# Revit family: FP-Revit20-RS32A72UI-FrenchDoorFridgeFreezer-0-90005071A-US-CA
name_source: partatom
category: Specialty Equipment
units: mm (PartAtom-declared; Revit-internal decimal feet)

## family parameters
Always vertical = Yes
Cut with Voids When Loaded = Yes
OmniClass Number = 23.40.40.11.11.17
OmniClass Title = Refrigerator-Freezer
Part Type = Normal
Room Calculation Point = No
Round Connector Dimension = Use Diameter
Shared = No
Work Plane-Based = No

## types (1)
- FP-Revit20-RS32A72UI-FrenchDoorFridgeFreezer-0-90005071A-US-CA
    Cavity - Depth = 635 mm  [stored 2.08333 ft]
    Cavity - Height = 1829 mm  [stored 6.00066 ft]
    Cavity - Width = 813 mm  [stored 2.66732 ft]
    Chassis - Depth = 561 mm
    Chassis - Height = 1788 mm
    Chassis - Width = 790 mm  [stored 2.59186 ft]
    Connector Description - Electrical = 115 V, 60 Hz, 10 A circuit
    Connector Description - Water = 13mm (1/2") or 19mm (3/4") BSP threaded water connection 6.35mm LLDPE tubing
    Default Elevation = 0 mm  [stored 0 ft]
    Description = Integrated French Door Refrigerator Freezer, Ice & Water
    Handle Style - Contemporary Round (AHSRS80A) = Yes
    Handle Style - Contemporary Square (AHD3RS80A) = Yes
    Handle Style - Contemporary Square Fine (AHD5RD80A) = Yes
    Handle Style - Contemporary Square Fine Black (AHD5RD80AB) = Yes
    Manufacturer = Fisher & Paykel Appliances
    Material - Body = Fisher & Paykel - Grey
    Material - Connections = Fisher & Paykel - Black
    Material - Door Front = Fisher & Paykel - Stainless Steel
    Material - Door Structure = Fisher & Paykel - White
    Material - Rollers and Feet = Fisher & Paykel - Black
    Material - Trim = Fisher & Paykel - Stainless Steel
    Model = RS32A72UI
    Product - Depth = 604 mm  [stored 1.98163 ft]
    Product - Height = 1825 mm  [stored 5.98753 ft]
    Product - Width = 796 mm  [stored 2.61155 ft]
    Stainless Steel Door Panels (RD80AU) = Yes
    URL = www.fisherpaykel.com
    Visibility - Clearance Required = No
    Visibility - Visibility Control Note = No
    Visibility - Water Dispenser = Yes

note: [stored X ft] marks values corroborated as IEEE doubles in the binary element streams (Revit-internal decimal feet)

## geometry (parser evidence)
native form markers: Sweep x17
no freeform markers — native parametric forms only
